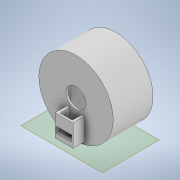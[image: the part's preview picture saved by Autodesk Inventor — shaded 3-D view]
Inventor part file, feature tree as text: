
AUTODESK INVENTOR PART (.ipt)
format: ipt  version: 2022.2 (Build 262287000, 287)  size: 295,424 bytes
history: native  units: mm
features: sketch x8, extrude x7, other x4, reference x4, projected_geometry x3, hole x2, plane x1
ambient origin geometry x8: Origin, YZ Plane, XZ Plane, XY Plane, X Axis, Y Axis, Z Axis, Center Point
bodies: Solid1 (feature_tree)
feature tree (29):
  other  "Motor.ipt"
  extrude  "Extrusion1"  Depth=4.0mm
  extrude  "Extrusion2"  TaperAngle=0.0deg  [1 undecoded]
  extrude  "Extrusion8"  Depth=10.0mm
  extrude  "Extrusion9"  Depth=2.0mm
  extrude  "Extrusion10"  Depth=2.4mm
  plane  "Work Plane6"
  hole  "Hole2"  [1 undecoded]
  hole  "Hole3"  [1 undecoded]
  extrude  "Extrusion11"  Depth=5.1mm
  extrude  "Extrusion12"  Depth=0.5mm
  reference  "Reference1"
  reference  "Reference2"
  sketch  "Sketch2"  dims[d0=4.0mm d1=7.0mm d6=3.2mm]
  reference  "Reference4"
  reference  "Reference5"
  projected_geometry  "Projected Loop11"
  sketch  "Sketch11"  dims[d8=0.0mm d15=0.0mm]
  sketch  "Sketch12"  dims[d35=10.0mm d51=0.3mm]
  sketch  "Sketch13"  dims[d53=2.0mm d55=2.5mm]
  sketch  "Sketch14"  dims[d57=6.2mm d58=2.4mm]
  projected_geometry  "Projected Loop14"
  sketch  "Sketch15"  dims[d59=1.0mm d60=0.0mm d61=8.16mm]
  sketch  "Sketch16"  dims[d62=5.1mm d63=0.0mm d64=8.16mm]
  sketch  "Sketch17"  dims[d65=10.0mm d66=0.0mm d67=5.1mm d68=2.04mm d69=5.8mm d70=2.6mm d71=3.2mm d72=6.0mm d73=6.0mm d74=3.0mm d75=90.0deg d76=8.0mm d77=0.0mm d78=3.2mm d79=6.0mm d80=6.0mm d81=2.0mm d82=90.0deg d83=8.0mm d84=0.0mm d85=9.0mm d86=5.25mm d87=0.25mm d88=0.0mm d89=0.0mm d90=2.0mm d91=13.4mm d93=0.6mm d94=0.0mm d28=0.5mm d29=0.872665mm d30=0.5mm d31=0.872665mm d49=0.5mm d50=0.872665mm d52=0.872665mm]
  projected_geometry  "Projected Loop16"
  other  "<userpath>\Documents\Inventor\Wire Bender\Assembly.iam"
  other  "Assembly.iam"
  other  "Tool Head:1"
note: 3 required parameter values undecoded (feature->parameter linkage not recoverable at this tier; creation-order binding heuristic only, values carry confidence <= 0.55)
